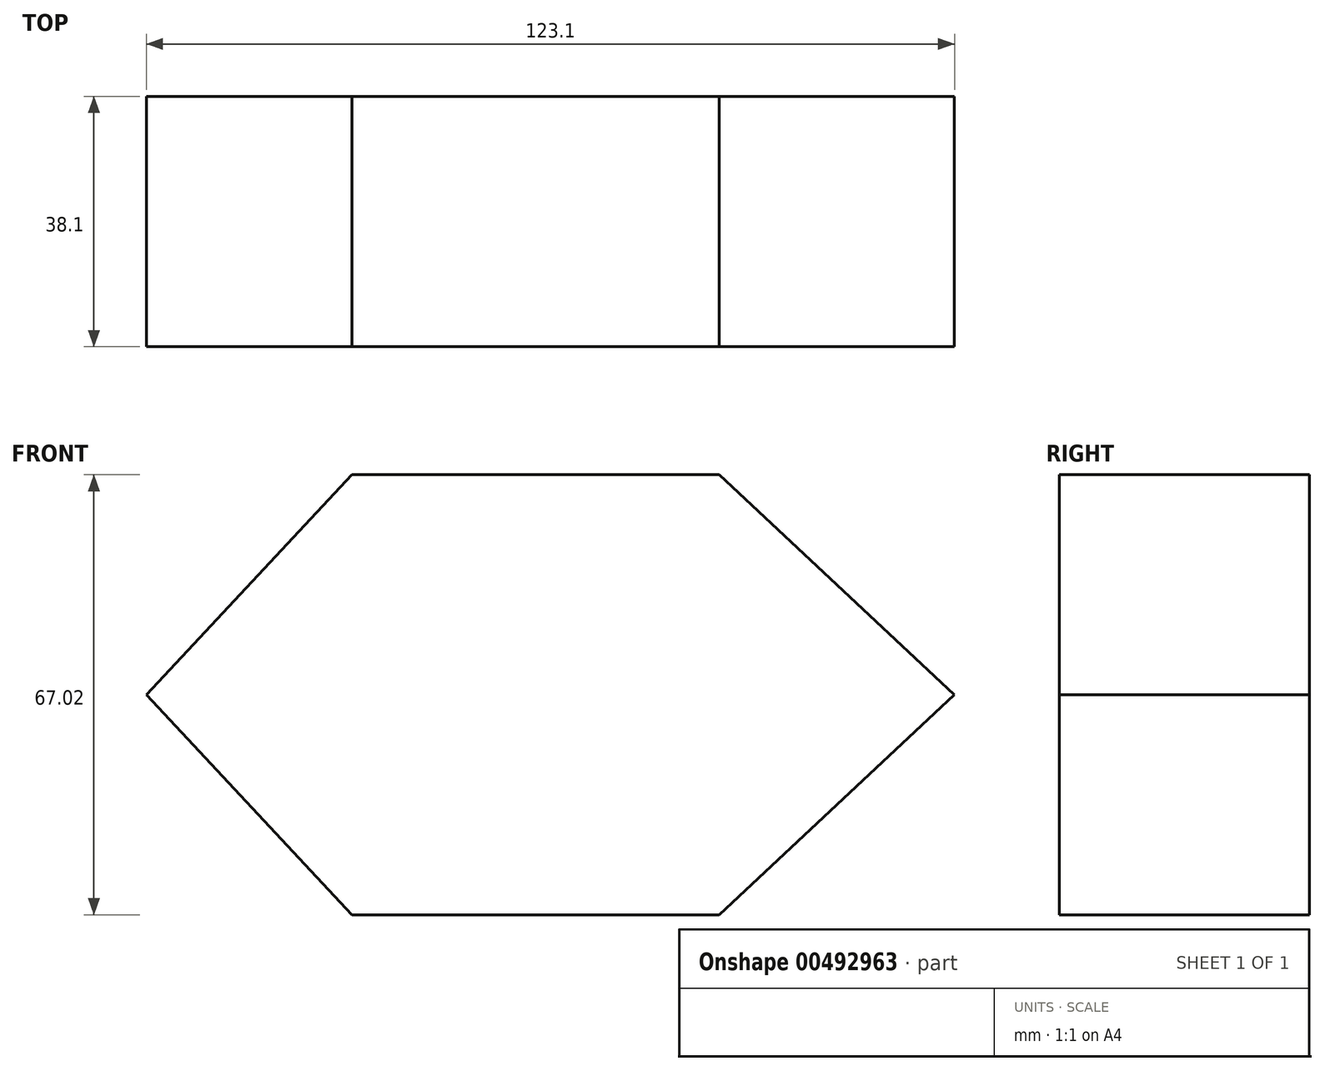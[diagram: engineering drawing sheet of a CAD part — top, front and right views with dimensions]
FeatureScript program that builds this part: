
annotation { "Feature Type Name" : "Feature", "Feature Type Description" : "" }
export const myFeature = defineFeature(function(context is Context, id is Id, definition is map)
    precondition{}
    {
        {
            var Q0;
            Q0=qCreatedBy(makeId("Front.planeOp"),FACE);
            var sketch = newSketch(context, id + "F0", { "sketchPlane" : qUnion([Q0])});
            skLineSegment(sketch, "E0", {"start": v(67.68, -4.1) * mm, "end": v(36.22, -33.5) * mm});
            skLineSegment(sketch, "E1", {"start": v(36.22, -33.5) * mm, "end": v(-19.7, -33.5) * mm});
            skLineSegment(sketch, "E2", {"start": v(-19.7, -33.5) * mm, "end": v(-47.2, -4.1) * mm});
            skLineSegment(sketch, "E3.MirrorCS", {"start": v(-19.7, 33.5) * mm, "end": v(-47.2, 4.1) * mm});
            skLineSegment(sketch, "E4.MirrorCS", {"start": v(36.22, 33.5) * mm, "end": v(-19.7, 33.5) * mm});
            skLineSegment(sketch, "E5.MirrorCS", {"start": v(67.68, 4.1) * mm, "end": v(36.22, 33.5) * mm});
            skLineSegment(sketch, "E6", {"start": v(-47.2, 4.1) * mm, "end": v(-51.03, 0) * mm});
            skLineSegment(sketch, "E7", {"start": v(-51.03, 0) * mm, "end": v(-47.2, -4.1) * mm});
            skLineSegment(sketch, "E8", {"start": v(67.68, -4.1) * mm, "end": v(72.07, 0) * mm});
            skLineSegment(sketch, "E9", {"start": v(72.07, 0) * mm, "end": v(67.68, 4.1) * mm});
            skSolve(sketch);
        }
        {
            var Q0;
            Q0=makeQuery(id+"F0.imprint","IMPRINT",FACE,{"disambiguationData":[TD([[makeQuery(id+"F0.imprint","IMPRINT",EDGE,{"derivedFrom":sQuery(id+"F0.wireOp",EDGE,"E0")}),-1.0]])]});
            extrude(context, id + "F1", {"entities" : qUnion([Q0]), "depth" : 38.1 * mm, "offsetDistance" : 25.4 * mm});
        }
    });
